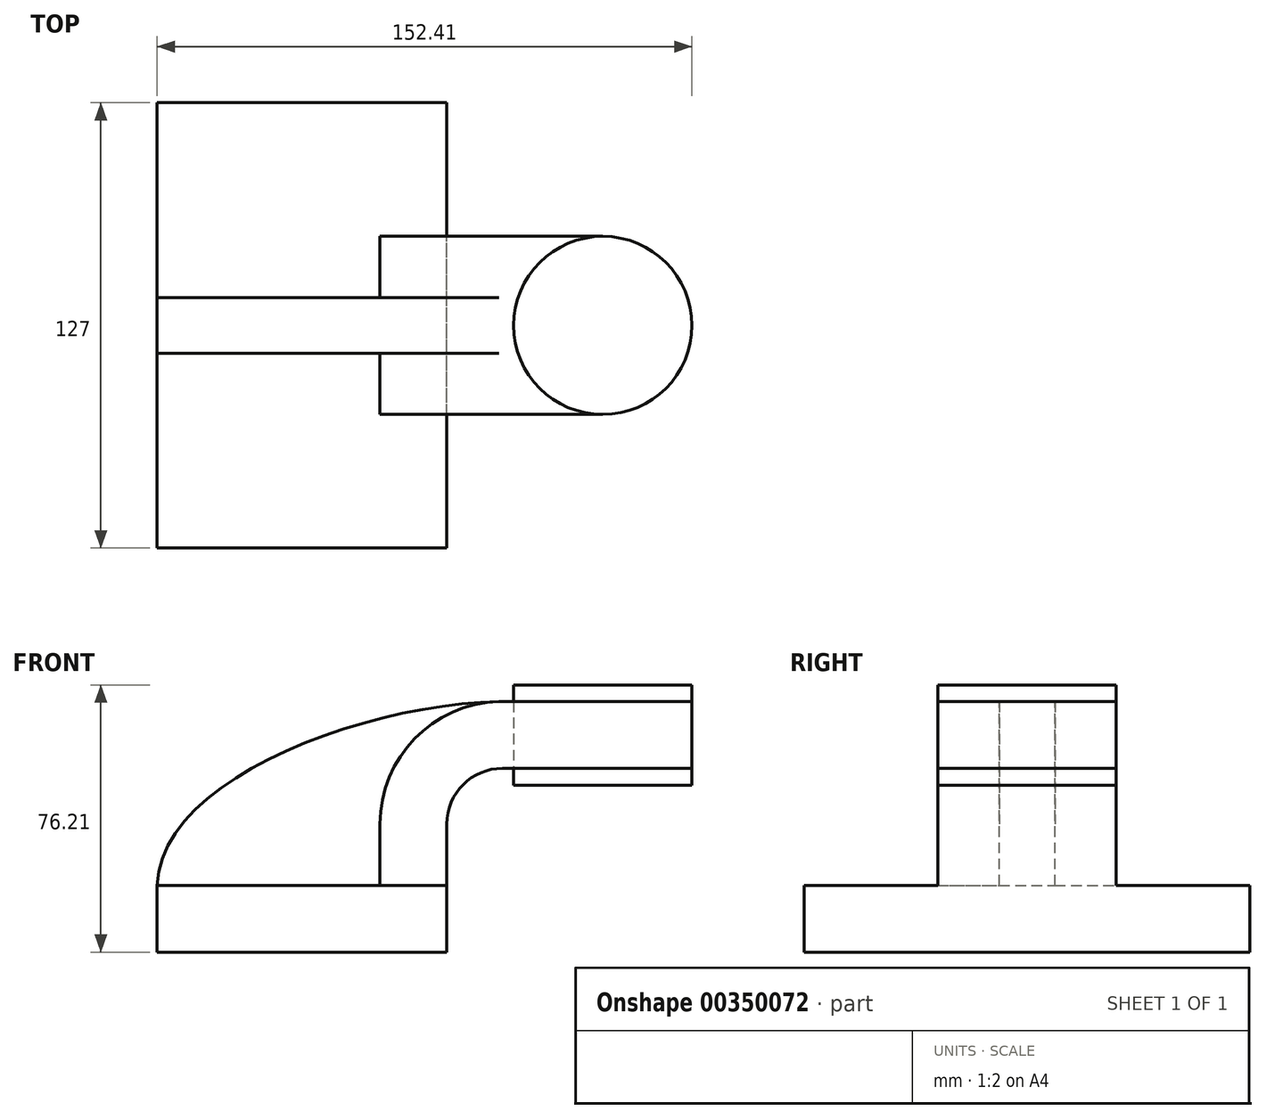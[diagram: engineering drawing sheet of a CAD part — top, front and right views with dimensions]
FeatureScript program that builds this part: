
annotation { "Feature Type Name" : "Feature", "Feature Type Description" : "" }
export const myFeature = defineFeature(function(context is Context, id is Id, definition is map)
    precondition{}
    {
        {
            var Q0;
            Q0=qCreatedBy(makeId("Front.planeOp"),FACE);
            var sketch = newSketch(context, id + "F0", { "sketchPlane" : qUnion([Q0])});
            skLineSegment(sketch, "E0.bottom", {"start": v(-41.27, -9.53) * mm, "end": v(41.28, -9.53) * mm});
            skLineSegment(sketch, "E0.top", {"start": v(-41.28, 9.53) * mm, "end": v(41.28, 9.53) * mm});
            skLineSegment(sketch, "E0.left", {"start": v(-41.28, -9.53) * mm, "end": v(-41.28, 9.53) * mm});
            skLineSegment(sketch, "E0.right", {"start": v(41.28, -9.53) * mm, "end": v(41.28, 9.53) * mm});
            skPoint(sketch, "E0.middle", {"position": v(0, 0) * mm});
            skLineSegment(sketch, "E1.bottom", {"start": v(111.13, 66.68) * mm, "end": v(60.32, 66.68) * mm});
            skLineSegment(sketch, "E1.top", {"start": v(111.13, 38.1) * mm, "end": v(60.32, 38.1) * mm});
            skLineSegment(sketch, "E1.left", {"start": v(111.12, 66.68) * mm, "end": v(111.12, 38.1) * mm});
            skLineSegment(sketch, "E1.right", {"start": v(60.32, 66.68) * mm, "end": v(60.32, 38.1) * mm});
            skPoint(sketch, "E1.middle", {"position": v(85.73, 52.39) * mm});
            skLineSegment(sketch, "E2", {"start": v(41.27, 9.53) * mm, "end": v(41.27, 27) * mm});
            skArc(sketch, "E3", {"start": v(41.27, 27) * mm, "mid": v(45.92, 38.23) * mm, "end": v(57.15, 42.88) * mm});
            skLineSegment(sketch, "E4", {"start": v(57.15, 42.88) * mm, "end": v(85.73, 42.88) * mm});
            skPoint(sketch, "E4.endSnap0", {"position": v(85.73, 38.1) * mm});
            skLineSegment(sketch, "E5.0", {"start": v(57.15, 61.93) * mm, "end": v(85.73, 61.93) * mm});
            skArc(sketch, "E5.1", {"start": v(22.22, 27) * mm, "mid": v(32.45, 51.7) * mm, "end": v(57.15, 61.93) * mm});
            skLineSegment(sketch, "E5.2", {"start": v(22.22, 9.53) * mm, "end": v(22.22, 27) * mm});
            skLineSegment(sketch, "E6", {"start": v(85.73, 38.1) * mm, "end": v(85.73, 66.68) * mm});
            skLineSegment(sketch, "E7", {"start": v(22.22, 9.53) * mm, "end": v(41.28, 9.53) * mm});
            skFitSpline(sketch, "E8", {"points": [v(-41.28, 9.53) * mm, v(57.15, 61.93) * mm], "startDerivative": vector(2.42, 90.47) * mm, "endDerivative": vector(118.23, 1.16) * mm});
            skSolve(sketch);
        }
        {
            var Q0;
            Q0=makeQuery(id+"F0.imprint","IMPRINT",FACE,{"disambiguationData":[TD([[makeQuery(id+"F0.imprint","IMPRINT",EDGE,{"derivedFrom":sQuery(id+"F0.wireOp",EDGE,"E0.bottom")}),1.0]])]});
            extrude(context, id + "F1", {"entities" : qUnion([Q0]), "endBound" : BoundingType.SYMMETRIC, "depth" : 127 * mm});
        }
        {
            var Q0;
            Q0=makeQuery(id+"F0.imprint","IMPRINT",FACE,{"disambiguationData":[TD([[makeQuery(id+"F0.imprint","IMPRINT",EDGE,{"derivedFrom":sQuery(id+"F0.wireOp",EDGE,"E2")}),1.0]])]});
            extrude(context, id + "F2", {"entities" : qUnion([Q0]), "operationType" : NewBodyOperationType.ADD, "endBound" : BoundingType.SYMMETRIC, "depth" : 50.8 * mm});
        }
        {
            var Q0;
            {var subQ0=sQuery(id+"F0.wireOp",EDGE,"E0.top");Q0=makeQuery(id+"F0.imprint","IMPRINT",FACE,{"disambiguationData":[TD([[makeQuery(id+"F0.imprint","IMPRINT",EDGE,{"derivedFrom":subQ0}),1.0]])]});}
            extrude(context, id + "F3", {"entities" : qUnion([Q0]), "operationType" : NewBodyOperationType.ADD, "endBound" : BoundingType.SYMMETRIC, "depth" : 15.88 * mm});
        }
        {
            var Q0;
            Q0=makeQuery(id+"F2.opExtrude","SWEPT_FACE",FACE,{"disambiguationData":[OSD([sQuery(id+"F0.wireOp",EDGE,"E1.right")])]});
            extrude(context, id + "F4", {"entities" : qUnion([Q0]), "operationType" : NewBodyOperationType.ADD, "depth" : 50.8 * mm});
        }
        {
            var Q0;
            {var subQ0=sQuery(id+"F0.wireOp",EDGE,"E1.left");Q0=makeQuery(id+"F0.imprint","IMPRINT",FACE,{"disambiguationData":[TD([[makeQuery(id+"F0.imprint","IMPRINT",EDGE,{"derivedFrom":subQ0}),-1.0]])]});}
            var Q1;
            Q1=sQuery(id+"F0.wireOp",EDGE,"E6");
            revolve(context, id + "F5", {"entities" : qUnion([Q0]), "axis" : qUnion([Q1]), "revolveType" : RevolveType.FULL});
        }
        {
            var Q0;
            {var subQ0=sQuery(id+"F0.wireOp",EDGE,"E1.right");Q0=makeQuery(id+"F4.opExtrude","CAP_EDGE",EDGE,{"disambiguationData":[OSD([subQ0]),TDD([makeQuery(id+"F2.opExtrude","CAP_EDGE",EDGE,{"disambiguationData":[OSD([subQ0])],"isStart":false})])],"isStart":false});}
            var Q1;
            {var subQ0=sQuery(id+"F0.wireOp",EDGE,"E1.right");Q1=makeQuery(id+"F4.opExtrude","CAP_EDGE",EDGE,{"disambiguationData":[OSD([subQ0]),TDD([makeQuery(id+"F2.opExtrude","CAP_EDGE",EDGE,{"disambiguationData":[OSD([subQ0])],"isStart":true})])],"isStart":false});}
            fillet(context, id + "F6", {"entities" : qUnion([Q0, Q1]), "radius" : 25.4 * mm, "tangentPropagation" : true, "allowEdgeOverflow" : false});
        }
    });
